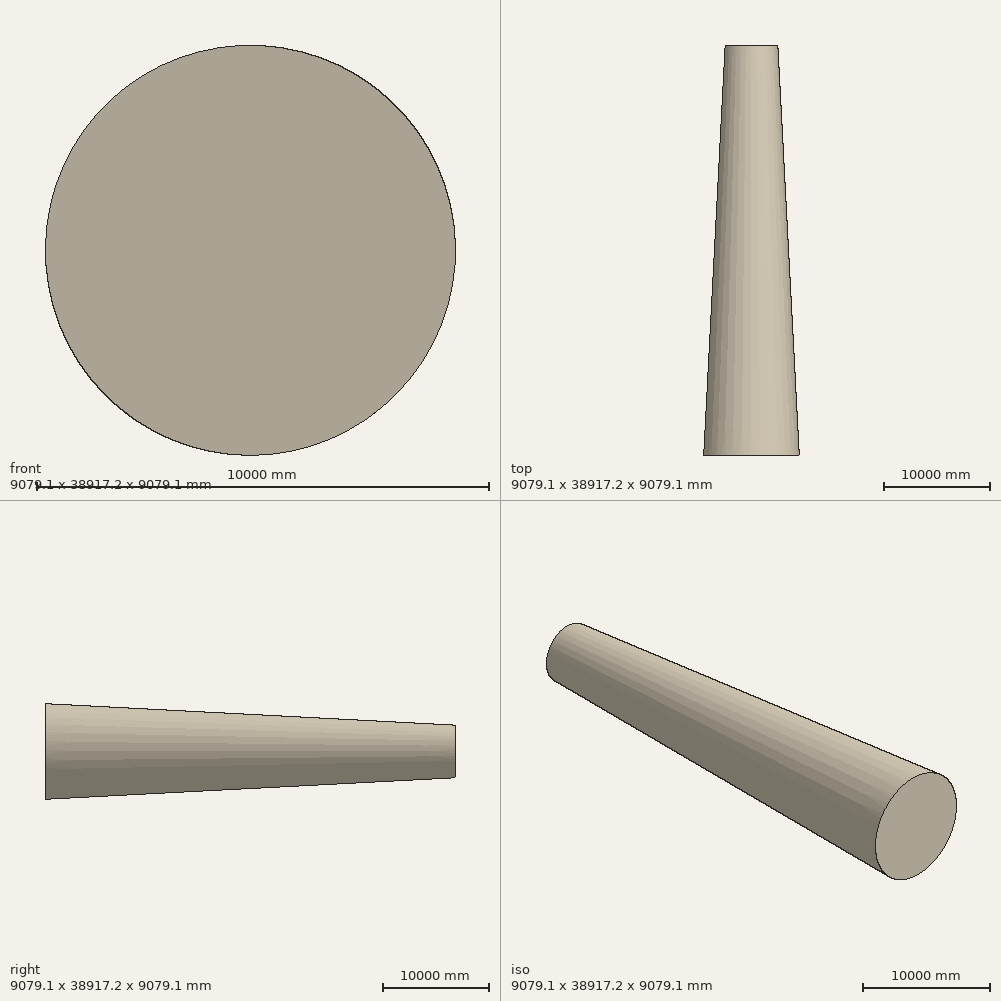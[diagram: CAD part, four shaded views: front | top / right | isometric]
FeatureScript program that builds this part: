
annotation { "Feature Type Name" : "Feature", "Feature Type Description" : "" }
export const myFeature = defineFeature(function(context is Context, id is Id, definition is map)
    precondition{}
    {
        {
            var Q0;
            Q0=qCreatedBy(makeId("Front.planeOp"),FACE);
            var sketch = newSketch(context, id + "F0", { "sketchPlane" : qUnion([Q0])});
            skCircle(sketch, "E0", {"center": v(0, 0) * mm, "radius": 2500 * mm});
            skSolve(sketch);
        }
        {
            var Q0;
            Q0 = qSketchRegion(id + "F0", true);
            var Q1;
            Q1=makeQuery(id+"F0.imprint","IMPRINT",FACE,{"disambiguationData":[TD([[makeQuery(id+"F0.imprint","IMPRINT",EDGE,{"derivedFrom":sQuery(id+"F0.wireOp",EDGE,"E0")}),1.0]])]});
            extrude(context, id + "F1", {"entities" : qUnion([Q0, Q1]), "depth" : 38917.15 * mm, "hasDraft" : true, "draftAngle" : 3 * degree});
        }
    });
